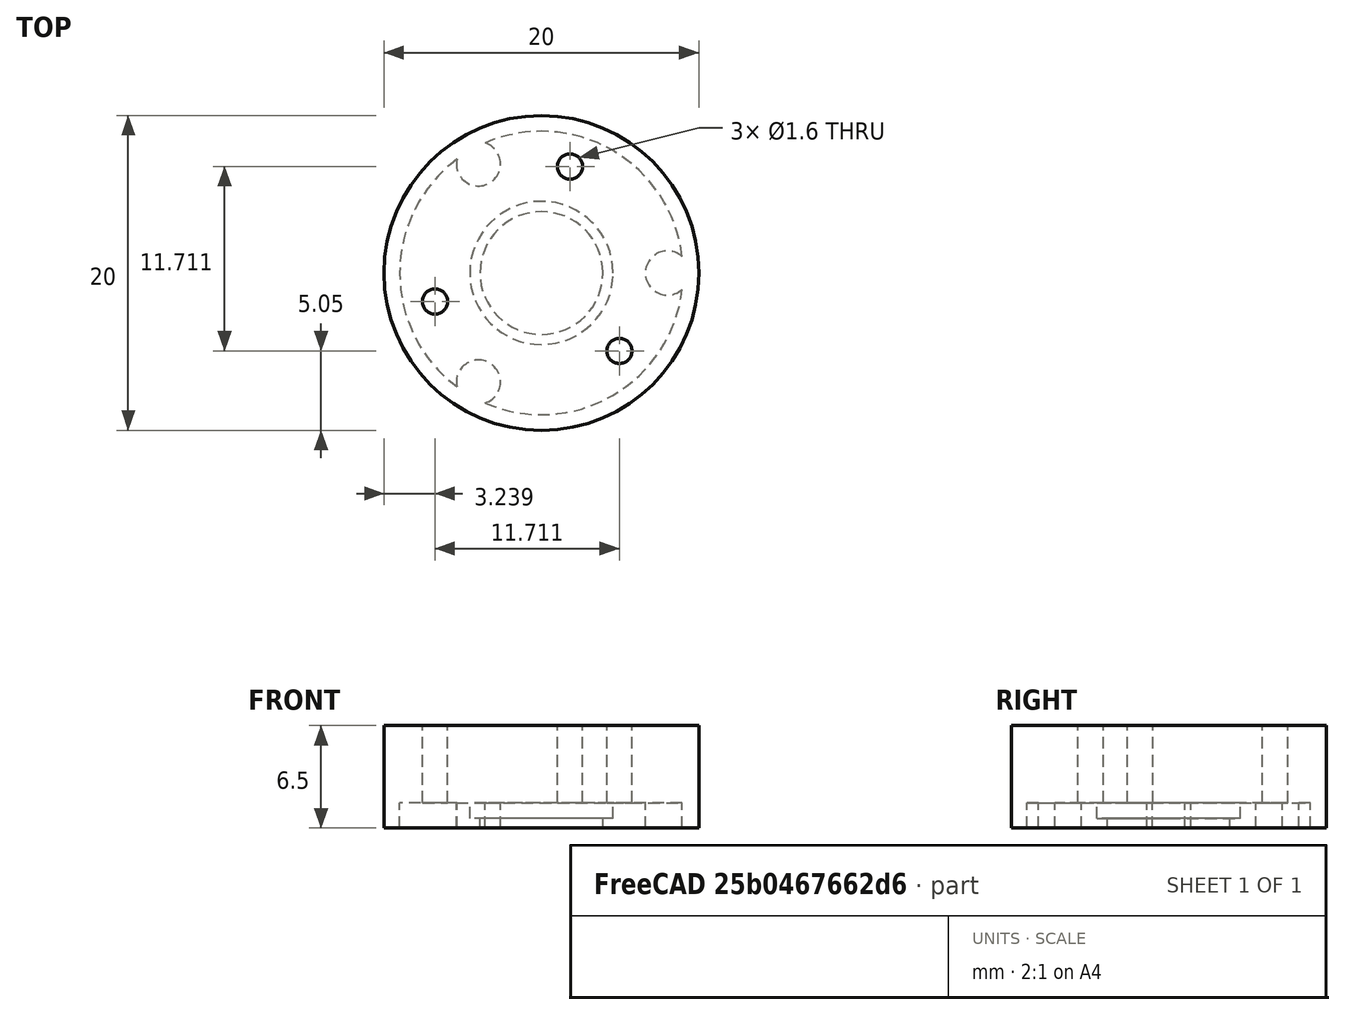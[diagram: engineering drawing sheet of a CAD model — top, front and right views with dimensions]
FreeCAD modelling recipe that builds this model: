
FCSTD DOCUMENT  (FreeCAD 0.18R16033 (Git))
Label: three_piece_mould
License: All rights reserved
LicenseURL: http://en.wikipedia.org/wiki/All_rights_reserved
objects: Part::Cylinder×6, Part::Cut×3, Part::FeaturePython×2, Part::MultiFuse×1
note: 12 computed .brp shape members not serialized (recipe doc carries the construction recipe); baked Part::Feature solids carry a one-line shape summary decoded from their .brp

FEATURE [Part::Cylinder] Cylinder043  label="Cylinder025"
  Angle = 360
  AttacherType = Attacher::AttachEngine3D
  Height = 6.5
  Radius = 10
FEATURE [Part::Cylinder] Cylinder023  label="MountPlateBody"
  Angle = 360
  AttacherType = Attacher::AttachEngine3D
  Height = 1.59
  Radius = 9
FEATURE [Part::Cylinder] Cylinder024  label="Cylinder016"
  Angle = 360
  AttacherType = Attacher::AttachEngine3D
  Height = 10
  Placement = pos=(8,0,0) rot=(0,0,1;0rad)
  Radius = 1.4
FEATURE [Part::FeaturePython] Array  # Draft array (typed FeaturePython)
  Angle = 360
  ArrayType = 1
  Axis = (0,0,1)
  Base = -> Cylinder024
  Center = (0,0,0)
  Fuse = false
  IntervalAxis = (0,0,0)
  IntervalX = (1,0,0)
  IntervalY = (0,1,0)
  IntervalZ = (0,0,1)
  NumberPolar = 3
  NumberX = 2
  NumberY = 2
  NumberZ = 1
FEATURE [Part::Cylinder] Cylinder026  label="MountPlateInnerHole"
  Angle = 360
  AttacherType = Attacher::AttachEngine3D
  Height = 10
  Radius = 3.9
FEATURE [Part::Cylinder] Cylinder027  label="MountPlateLip"
  Angle = 360
  AttacherType = Attacher::AttachEngine3D
  Height = 10
  Placement = pos=(0,0,0.6) rot=(0,0,1;0rad)
  Radius = 4.55
FEATURE [Part::MultiFuse] Fusion012
  Shapes = -> [Array,Cylinder027,Cylinder026]
FEATURE [Part::Cut] Cut013
  Base = -> Cylinder023
  Tool = -> Fusion012
FEATURE [Part::Cut] Cut014
  Base = -> Cylinder043
  Tool = -> Cut013
FEATURE [Part::Cylinder] Cylinder044  label="Cylinder026"
  Angle = 360
  AttacherType = Attacher::AttachEngine3D
  Height = 10
  Placement = pos=(7,0,0) rot=(0,0,1;0rad)
  Radius = 0.8
FEATURE [Part::FeaturePython] Array007  # Draft array (typed FeaturePython)
  Angle = 360
  ArrayType = 1
  Axis = (0,0,1)
  Base = -> Cylinder044
  Center = (0,0,0)
  Fuse = false
  IntervalAxis = (0,0,0)
  IntervalX = (1,0,0)
  IntervalY = (0,1,0)
  IntervalZ = (0,0,1)
  NumberPolar = 3
  NumberX = 2
  NumberY = 2
  NumberZ = 1
  Placement = pos=(0,0,0) rot=(0,0,-1;0.785398rad)
FEATURE [Part::Cut] Cut015
  Base = -> Cut014
  Tool = -> Array007
